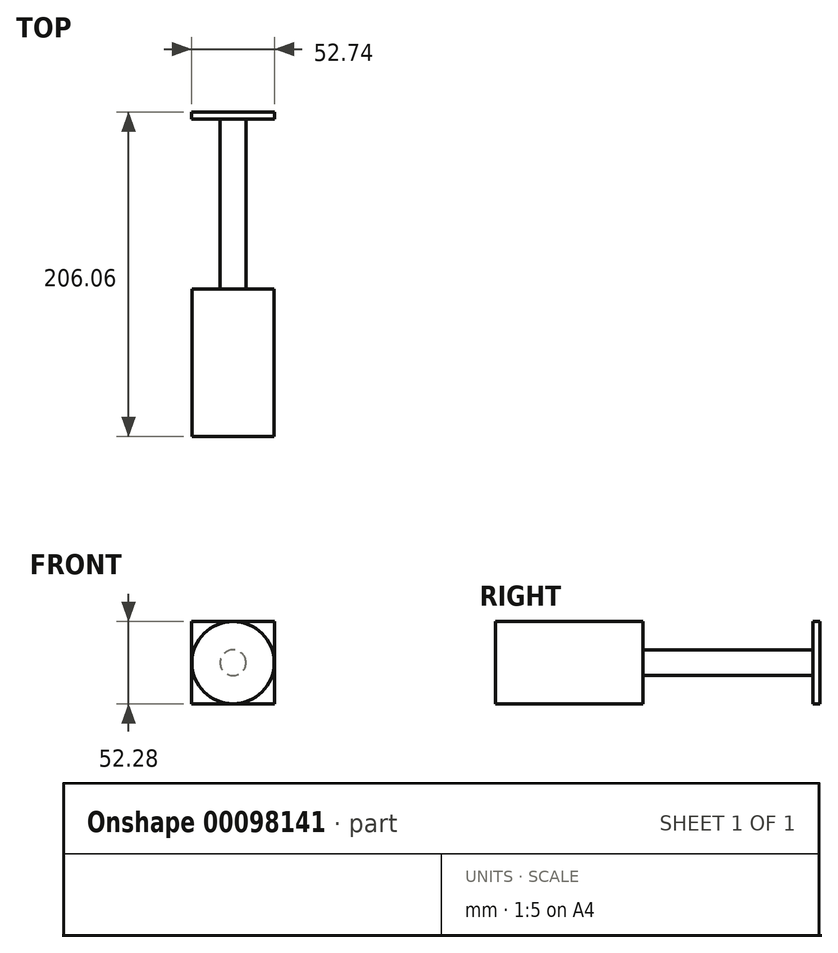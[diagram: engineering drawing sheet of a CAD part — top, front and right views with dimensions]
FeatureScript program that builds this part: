
annotation { "Feature Type Name" : "Feature", "Feature Type Description" : "" }
export const myFeature = defineFeature(function(context is Context, id is Id, definition is map)
    precondition{}
    {
        {
            var Q0;
            Q0=qCreatedBy(makeId("Front.planeOp"),FACE);
            var sketch = newSketch(context, id + "F0", { "sketchPlane" : qUnion([Q0])});
            skCircle(sketch, "E0", {"center": v(0, 0) * mm, "radius": 26.12 * mm});
            skSolve(sketch);
        }
        {
            var Q0;
            Q0 = qSketchRegion(id + "F0", true);
            extrude(context, id + "F1", {"entities" : qUnion([Q0]), "depth" : 93.77 * mm});
        }
        {
            var Q0;
            Q0=makeQuery(id+"F1.opExtrude","CAP_FACE",FACE,{"disambiguationData":[OSD([sQuery(id+"F0.wireOp",EDGE,"E0")])],"isStart":true});
            var sketch = newSketch(context, id + "F2", { "sketchPlane" : qUnion([Q0])});
            skCircle(sketch, "E1", {"center": v(0, 0) * mm, "radius": 8.17 * mm});
            skSolve(sketch);
        }
        {
            var Q0;
            Q0 = qSketchRegion(id + "F2", true);
            extrude(context, id + "F3", {"entities" : qUnion([Q0]), "operationType" : NewBodyOperationType.ADD, "depth" : 107.9 * mm});
        }
        {
            var Q0;
            Q0=makeQuery(id+"F3.opExtrude","CAP_FACE",FACE,{"disambiguationData":[OSD([sQuery(id+"F2.wireOp",EDGE,"E1")])],"isStart":false});
            var sketch = newSketch(context, id + "F4", { "sketchPlane" : qUnion([Q0])});
            skLineSegment(sketch, "E2.bottom", {"start": v(26.37, 26.14) * mm, "end": v(-26.37, 26.14) * mm});
            skLineSegment(sketch, "E2.top", {"start": v(26.37, -26.14) * mm, "end": v(-26.37, -26.14) * mm});
            skLineSegment(sketch, "E2.left", {"start": v(26.37, 26.14) * mm, "end": v(26.37, -26.14) * mm});
            skLineSegment(sketch, "E2.right", {"start": v(-26.37, 26.14) * mm, "end": v(-26.37, -26.14) * mm});
            skPoint(sketch, "E2.middle", {"position": v(0, 0) * mm});
            skSolve(sketch);
        }
        {
            var Q0;
            Q0 = qSketchRegion(id + "F4", true);
            extrude(context, id + "F5", {"entities" : qUnion([Q0]), "operationType" : NewBodyOperationType.ADD, "depth" : 4.4 * mm});
        }
    });
